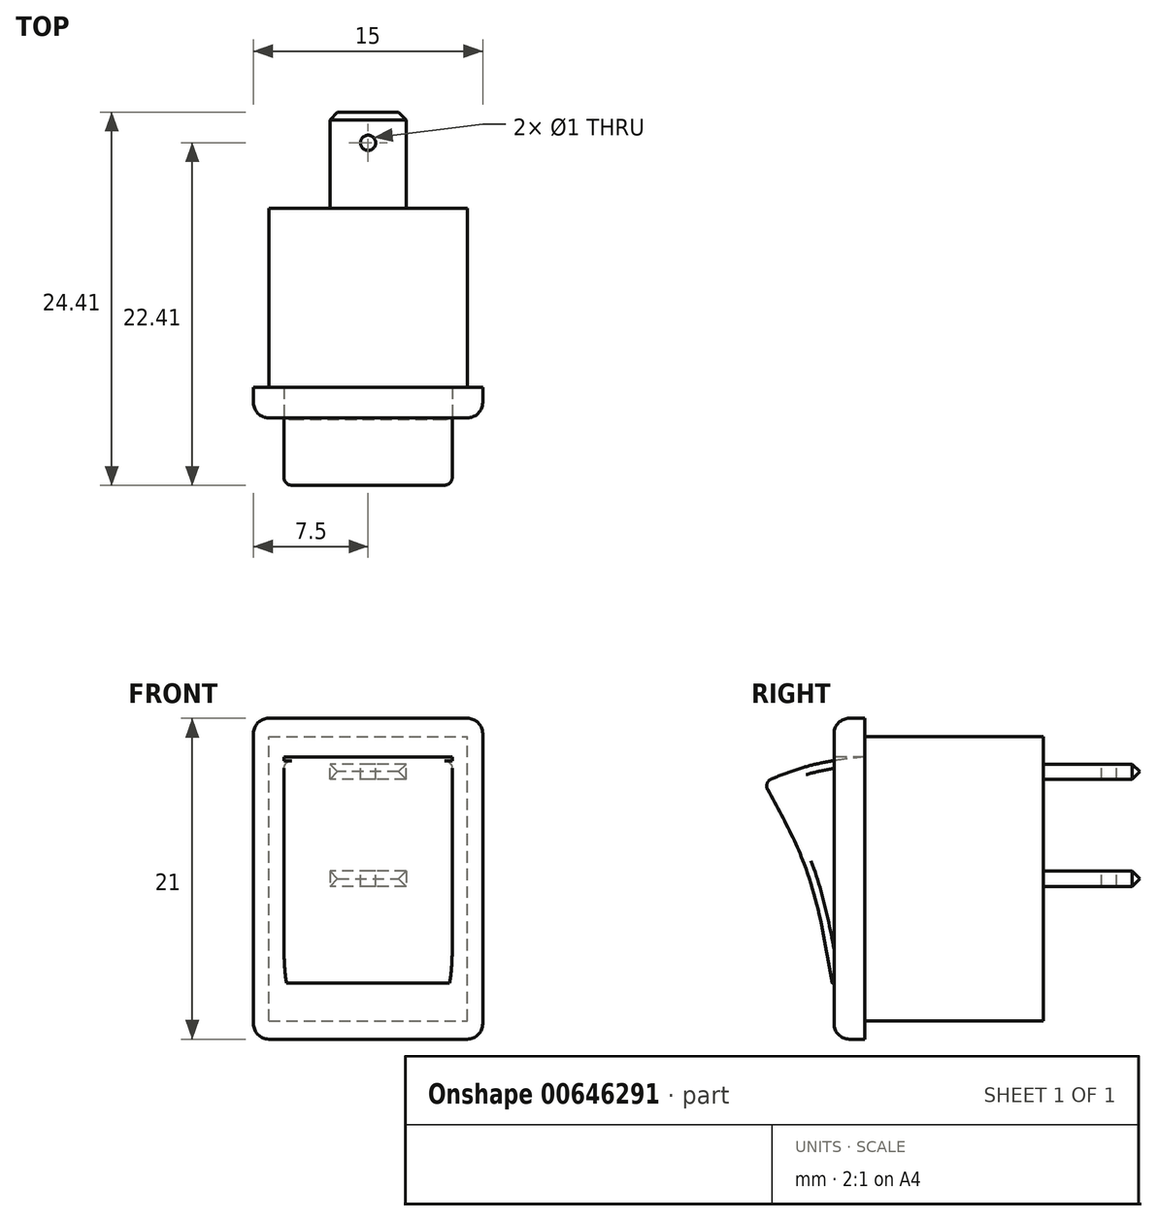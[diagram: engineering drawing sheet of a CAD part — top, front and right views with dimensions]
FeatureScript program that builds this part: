
annotation { "Feature Type Name" : "Feature", "Feature Type Description" : "" }
export const myFeature = defineFeature(function(context is Context, id is Id, definition is map)
    precondition{}
    {
        {
            var Q0;
            Q0=qCreatedBy(makeId("Front.planeOp"),FACE);
            var sketch = newSketch(context, id + "F0", { "sketchPlane" : qUnion([Q0])});
            skLineSegment(sketch, "E0.bottom", {"start": v(0, 0) * mm, "end": v(13, 0) * mm});
            skLineSegment(sketch, "E0.top", {"start": v(0, 18.6) * mm, "end": v(13, 18.6) * mm});
            skLineSegment(sketch, "E0.left", {"start": v(0, 0) * mm, "end": v(0, 18.6) * mm});
            skLineSegment(sketch, "E0.right", {"start": v(13, 0) * mm, "end": v(13, 18.6) * mm});
            skSolve(sketch);
        }
        {
            var Q0;
            Q0 = qSketchRegion(id + "F0", true);
            extrude(context, id + "F1", {"entities" : qUnion([Q0]), "oppositeDirection" : true, "depth" : 11.7 * mm, "offsetDistance" : 25 * mm});
        }
        {
            var Q0;
            Q0=qCreatedBy(makeId("Front.planeOp"),FACE);
            var sketch = newSketch(context, id + "F2", { "sketchPlane" : qUnion([Q0])});
            skLineSegment(sketch, "E1.bottom", {"start": v(-1, 19.8) * mm, "end": v(14, 19.8) * mm});
            skLineSegment(sketch, "E1.top", {"start": v(-1, -1.2) * mm, "end": v(14, -1.2) * mm});
            skLineSegment(sketch, "E1.left", {"start": v(-1, 19.8) * mm, "end": v(-1, -1.2) * mm});
            skLineSegment(sketch, "E1.right", {"start": v(14, 19.8) * mm, "end": v(14, -1.2) * mm});
            skSolve(sketch);
        }
        {
            var Q0;
            Q0 = qSketchRegion(id + "F2", true);
            extrude(context, id + "F3", {"entities" : qUnion([Q0]), "operationType" : NewBodyOperationType.ADD, "depth" : 2 * mm, "offsetDistance" : 25 * mm});
        }
        {
            var Q0;
            Q0=qCreatedBy(makeId("Right.planeOp"),FACE);
            var sketch = newSketch(context, id + "F4", { "sketchPlane" : qUnion([Q0])});
            skLineSegment(sketch, "E2", {"start": v(-2.13, 2.48) * mm, "end": v(0, 2.48) * mm});
            skFitSpline(sketch, "E3", {"points": [v(0, 17.28) * mm, v(-3.41, 16.75) * mm, v(-6.62, 15.62) * mm], "startDerivative": vector(-6.89, -0.75) * mm, "endDerivative": vector(-6.35, -2.56) * mm});
            skFitSpline(sketch, "E4", {"points": [v(-6.62, 15.62) * mm, v(-3.77, 9.76) * mm, v(-2.13, 2.48) * mm], "startDerivative": vector(6.55, -11.66) * mm, "endDerivative": vector(2.48, -14.59) * mm});
            skLineSegment(sketch, "E5", {"start": v(0, 17.28) * mm, "end": v(0, 2.48) * mm});
            skLineSegment(sketch, "E6.bottom", {"start": v(0, 17.28) * mm, "end": v(-3.97, 17.28) * mm});
            skLineSegment(sketch, "E6.top", {"start": v(0, 2.48) * mm, "end": v(-3.97, 2.48) * mm});
            skLineSegment(sketch, "E6.right", {"start": v(-3.97, 17.28) * mm, "end": v(-3.97, 2.48) * mm});
            skSolve(sketch);
        }
        {
            var Q0;
            {var subQ0=sQuery(id+"F4.wireOp",EDGE,"E6.bottom");Q0=makeQuery(id+"F4.imprint","IMPRINT",FACE,{"disambiguationData":[TD([[makeQuery(id+"F4.imprint","IMPRINT",EDGE,{"derivedFrom":subQ0}),1.0]])]});}
            var Q1;
            {var subQ0=sQuery(id+"F4.wireOp",EDGE,"E6.top");var subQ1=sQuery(id+"F4.wireOp",EDGE,"E4");var subQ2=makeQuery(id+"F4.imprint","INTERSECT",VERTEX,{"derivedFrom":[subQ1,subQ0]});Q1=makeQuery(id+"F4.imprint","IMPRINT",FACE,{"disambiguationData":[TD([[makeQuery(id+"F4.imprint","IMPRINT",EDGE,{"disambiguationData":[TD([[subQ2,1.0]])],"derivedFrom":subQ1}),-1.0]])]});}
            var Q2;
            {var subQ0=sQuery(id+"F4.wireOp",EDGE,"E5");Q2=makeQuery(id+"F4.imprint","IMPRINT",FACE,{"disambiguationData":[TD([[makeQuery(id+"F4.imprint","IMPRINT",EDGE,{"derivedFrom":subQ0}),-1.0]])]});}
            extrude(context, id + "F5", {"entities" : qUnion([Q0, Q1, Q2]), "operationType" : NewBodyOperationType.REMOVE, "depth" : 12 * mm, "offsetDistance" : 25 * mm, "hasSecondDirection" : true, "secondDirectionOppositeDirection" : false, "secondDirectionDepth" : 1 * mm});
        }
        {
            var Q0;
            {var subQ0=sQuery(id+"F4.wireOp",EDGE,"E5");Q0=makeQuery(id+"F4.imprint","IMPRINT",FACE,{"disambiguationData":[TD([[makeQuery(id+"F4.imprint","IMPRINT",EDGE,{"derivedFrom":subQ0}),-1.0]])]});}
            var Q1;
            {var subQ0=sQuery(id+"F4.wireOp",EDGE,"E4");var subQ1=sQuery(id+"F4.wireOp",EDGE,"E3");var subQ2=makeQuery(id+"F4.imprint","INTERSECT",VERTEX,{"derivedFrom":[subQ1,subQ0]});Q1=makeQuery(id+"F4.imprint","IMPRINT",FACE,{"disambiguationData":[TD([[makeQuery(id+"F4.imprint","IMPRINT",EDGE,{"disambiguationData":[TD([[subQ2,1.0]])],"derivedFrom":subQ1}),1.0]])]});}
            extrude(context, id + "F6", {"entities" : qUnion([Q0, Q1]), "operationType" : NewBodyOperationType.ADD, "depth" : 12 * mm, "offsetDistance" : 25 * mm, "hasSecondDirection" : true, "secondDirectionOppositeDirection" : false, "secondDirectionDepth" : 1 * mm});
        }
        {
            var Q0;
            Q0=makeQuery(id+"F3.opExtrude","SWEPT_EDGE",EDGE,{"disambiguationData":[OSD([sQuery(id+"F2.wireOp",EDGE,"E1.top"),sQuery(id+"F2.wireOp",EDGE,"E1.right")])]});
            var Q1;
            Q1=makeQuery(id+"F3.opExtrude","SWEPT_EDGE",EDGE,{"disambiguationData":[OSD([sQuery(id+"F2.wireOp",EDGE,"E1.top"),sQuery(id+"F2.wireOp",EDGE,"E1.left")])]});
            var Q2;
            Q2=makeQuery(id+"F3.opExtrude","SWEPT_EDGE",EDGE,{"disambiguationData":[OSD([sQuery(id+"F2.wireOp",EDGE,"E1.bottom"),sQuery(id+"F2.wireOp",EDGE,"E1.left")])]});
            var Q3;
            Q3=makeQuery(id+"F3.opExtrude","SWEPT_EDGE",EDGE,{"disambiguationData":[OSD([sQuery(id+"F2.wireOp",EDGE,"E1.bottom"),sQuery(id+"F2.wireOp",EDGE,"E1.right")])]});
            var Q4;
            Q4=makeQuery(id+"F3.opExtrude","CAP_EDGE",EDGE,{"disambiguationData":[OSD([sQuery(id+"F2.wireOp",EDGE,"E1.right")])],"isStart":false});
            var Q5;
            Q5=makeQuery(id+"F3.opExtrude","CAP_EDGE",EDGE,{"disambiguationData":[OSD([sQuery(id+"F2.wireOp",EDGE,"E1.top")])],"isStart":false});
            var Q6;
            Q6=makeQuery(id+"F3.opExtrude","CAP_EDGE",EDGE,{"disambiguationData":[OSD([sQuery(id+"F2.wireOp",EDGE,"E1.left")])],"isStart":false});
            var Q7;
            Q7=makeQuery(id+"F3.opExtrude","CAP_EDGE",EDGE,{"disambiguationData":[OSD([sQuery(id+"F2.wireOp",EDGE,"E1.bottom")])],"isStart":false});
            fillet(context, id + "F7", {"entities" : qUnion([Q0, Q1, Q2, Q3, Q4, Q5, Q6, Q7]), "radius" : 1 * mm, "tangentPropagation" : true, "allowEdgeOverflow" : false});
        }
        {
            var Q0;
            {var subQ0=sQuery(id+"F4.wireOp",EDGE,"E3");Q0=makeQuery(id+"F6.boolean.opBoolean","SPLIT",EDGE,{"disambiguationData":[topologyDisambiguationEdgeConnected([makeQuery(id+"F6.opExtrude","CAP_FACE",FACE,{"disambiguationData":[OSD([subQ0,sQuery(id+"F4.wireOp",EDGE,"E4"),sQuery(id+"F4.wireOp",EDGE,"E6.top"),sQuery(id+"F4.wireOp",EDGE,"E5")])],"isStart":true})])],"derivedFrom":makeQuery(id+"F6.opExtrude","CAP_EDGE",EDGE,{"disambiguationData":[OSD([subQ0])],"isStart":true})});}
            var Q1;
            Q1=makeQuery(id+"F6.opExtrude","CAP_EDGE",EDGE,{"disambiguationData":[OSD([sQuery(id+"F4.wireOp",EDGE,"E4")])],"isStart":true});
            var Q2;
            Q2=makeQuery(id+"F6.opExtrude","SWEPT_EDGE",EDGE,{"disambiguationData":[OSD([sQuery(id+"F4.wireOp",EDGE,"E3"),sQuery(id+"F4.wireOp",EDGE,"E4")])]});
            var Q3;
            Q3=makeQuery(id+"F6.opExtrude","CAP_EDGE",EDGE,{"disambiguationData":[OSD([sQuery(id+"F4.wireOp",EDGE,"E4")])],"isStart":false});
            var Q4;
            {var subQ0=sQuery(id+"F4.wireOp",EDGE,"E3");Q4=makeQuery(id+"F6.boolean.opBoolean","SPLIT",EDGE,{"disambiguationData":[topologyDisambiguationEdgeConnected([makeQuery(id+"F6.opExtrude","CAP_FACE",FACE,{"disambiguationData":[OSD([subQ0,sQuery(id+"F4.wireOp",EDGE,"E4"),sQuery(id+"F4.wireOp",EDGE,"E6.top"),sQuery(id+"F4.wireOp",EDGE,"E5")])],"isStart":false})])],"derivedFrom":makeQuery(id+"F6.opExtrude","CAP_EDGE",EDGE,{"disambiguationData":[OSD([subQ0])],"isStart":false})});}
            fillet(context, id + "F8", {"entities" : qUnion([Q0, Q1, Q2, Q3, Q4]), "radius" : 0.5 * mm, "tangentPropagation" : true, "allowEdgeOverflow" : false});
        }
        {
            var Q0;
            Q0=makeQuery(id+"F1.opExtrude","CAP_FACE",FACE,{"disambiguationData":[OSD([sQuery(id+"F0.wireOp",EDGE,"E0.bottom"),sQuery(id+"F0.wireOp",EDGE,"E0.top"),sQuery(id+"F0.wireOp",EDGE,"E0.left"),sQuery(id+"F0.wireOp",EDGE,"E0.right")])],"isStart":false});
            var sketch = newSketch(context, id + "F9", { "sketchPlane" : qUnion([Q0])});
            skLineSegment(sketch, "E7.bottom", {"start": v(-9, 9.8) * mm, "end": v(-4, 9.8) * mm});
            skLineSegment(sketch, "E7.top", {"start": v(-9, 8.8) * mm, "end": v(-4, 8.8) * mm});
            skLineSegment(sketch, "E7.left", {"start": v(-9, 9.8) * mm, "end": v(-9, 8.8) * mm});
            skLineSegment(sketch, "E7.right", {"start": v(-4, 9.8) * mm, "end": v(-4, 8.8) * mm});
            skLineSegment(sketch, "E8.bottom", {"start": v(-9, 15.8) * mm, "end": v(-4, 15.8) * mm});
            skLineSegment(sketch, "E8.top", {"start": v(-9, 16.8) * mm, "end": v(-4, 16.8) * mm});
            skLineSegment(sketch, "E8.left", {"start": v(-9, 15.8) * mm, "end": v(-9, 16.8) * mm});
            skLineSegment(sketch, "E8.right", {"start": v(-4, 15.8) * mm, "end": v(-4, 16.8) * mm});
            skSolve(sketch);
        }
        {
            var Q0;
            Q0 = qSketchRegion(id + "F9", true);
            extrude(context, id + "F10", {"entities" : qUnion([Q0]), "operationType" : NewBodyOperationType.ADD, "depth" : 6.3 * mm, "offsetDistance" : 25 * mm});
        }
        {
            var Q0;
            Q0=makeQuery(id+"F10.opExtrude","CAP_EDGE",EDGE,{"disambiguationData":[OSD([sQuery(id+"F9.wireOp",EDGE,"E8.right")])],"isStart":false});
            var Q1;
            Q1=makeQuery(id+"F10.opExtrude","CAP_EDGE",EDGE,{"disambiguationData":[OSD([sQuery(id+"F9.wireOp",EDGE,"E8.left")])],"isStart":false});
            var Q2;
            Q2=makeQuery(id+"F10.opExtrude","CAP_EDGE",EDGE,{"disambiguationData":[OSD([sQuery(id+"F9.wireOp",EDGE,"E7.right")])],"isStart":false});
            var Q3;
            Q3=makeQuery(id+"F10.opExtrude","CAP_EDGE",EDGE,{"disambiguationData":[OSD([sQuery(id+"F9.wireOp",EDGE,"E7.left")])],"isStart":false});
            var Q4;
            Q4=makeQuery(id+"F10.opExtrude","CAP_EDGE",EDGE,{"disambiguationData":[OSD([sQuery(id+"F9.wireOp",EDGE,"E8.top")])],"isStart":false});
            var Q5;
            Q5=makeQuery(id+"F10.opExtrude","CAP_EDGE",EDGE,{"disambiguationData":[OSD([sQuery(id+"F9.wireOp",EDGE,"E8.bottom")])],"isStart":false});
            var Q6;
            Q6=makeQuery(id+"F10.opExtrude","CAP_EDGE",EDGE,{"disambiguationData":[OSD([sQuery(id+"F9.wireOp",EDGE,"E7.bottom")])],"isStart":false});
            var Q7;
            Q7=makeQuery(id+"F10.opExtrude","CAP_EDGE",EDGE,{"disambiguationData":[OSD([sQuery(id+"F9.wireOp",EDGE,"E7.top")])],"isStart":false});
            chamfer(context, id + "F11", {"entities" : qUnion([Q0, Q1, Q2, Q3, Q4, Q5, Q6, Q7]), "width" : 0.5 * mm, "tangentPropagation" : true});
        }
        {
            var Q0;
            Q0=makeQuery(id+"F10.opExtrude","SWEPT_FACE",FACE,{"disambiguationData":[OSD([sQuery(id+"F9.wireOp",EDGE,"E8.top")])]});
            var sketch = newSketch(context, id + "F12", { "sketchPlane" : qUnion([Q0])});
            skPoint(sketch, "E9.centerSnap0", {"position": v(9, 14.6) * mm});
            skCircle(sketch, "E10", {"center": v(6.5, 16) * mm, "radius": 0.5 * mm});
            skSolve(sketch);
        }
        {
            var Q0;
            Q0 = qSketchRegion(id + "F12", true);
            extrude(context, id + "F13", {"entities" : qUnion([Q0]), "operationType" : NewBodyOperationType.REMOVE, "oppositeDirection" : true, "depth" : 25 * mm, "offsetDistance" : 25 * mm});
        }
    });
